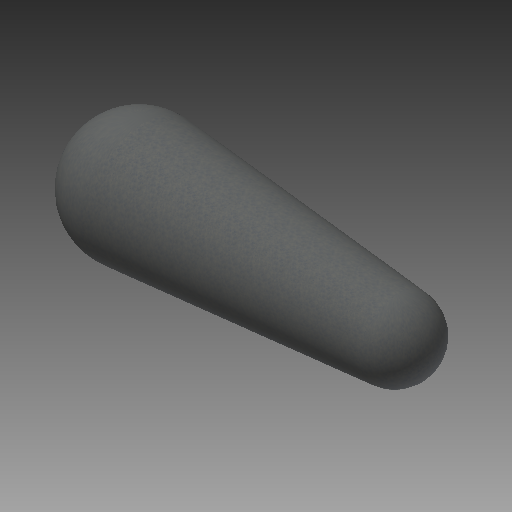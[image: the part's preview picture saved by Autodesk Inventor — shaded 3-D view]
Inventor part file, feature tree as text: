
AUTODESK INVENTOR PART (.ipt)
format: ipt  version: 2022 (Build 260153000, 153)  size: 224,256 bytes
history: native  units: mm (DEFAULTED — no unit token found)
features: other x1, revolve x1, sketch x1
ambient origin geometry x8: Origin, YZ Plane, XZ Plane, XY Plane, X Axis, Y Axis, Z Axis, Center Point
bodies: Solid1 (feature_tree)
feature tree (3):
  other  "iMandy - 2D BODY"
  revolve  "Revolution1"  [1 undecoded]
  sketch  "Sketch1"  dims[d1=10.0mm d16=389.128mm d17=181.864mm d18=115.824mm d19=90.0deg]
note: 1 required parameter value undecoded (feature->parameter linkage not recoverable at this tier; creation-order binding heuristic only, values carry confidence <= 0.55)
